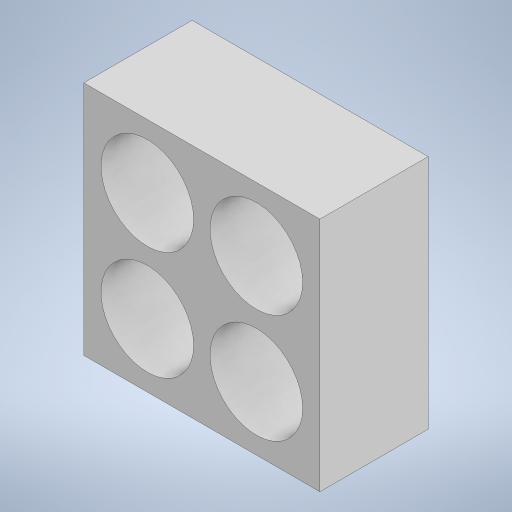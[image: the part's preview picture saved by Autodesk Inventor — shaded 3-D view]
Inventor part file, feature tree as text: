
AUTODESK INVENTOR PART (.ipt)
format: ipt  version: 2024 (Build 280153000, 153)  size: 217,600 bytes
history: native  units: in
note: dims shown in document units (in); Inventor stores cm internally (conversion verified against a paired STEP export)
features: extrude x1, sketch x1
ambient origin geometry x8: Origin, YZ Plane, XZ Plane, XY Plane, X Axis, Y Axis, Z Axis, Center Point
bodies: Solid1 (feature_tree)
feature tree (2):
  extrude  "Extrusion1"  Depth=1.0in
  sketch  "Sketch1"  dims[d3=0.855in d6=0.5867in d7=0.5867in d10=0.7874in d12=1.0067in d13=0.7874in d15=1.0067in d18=1.0in d19=0.0in d20=0.5866in d21=0.5866in]
